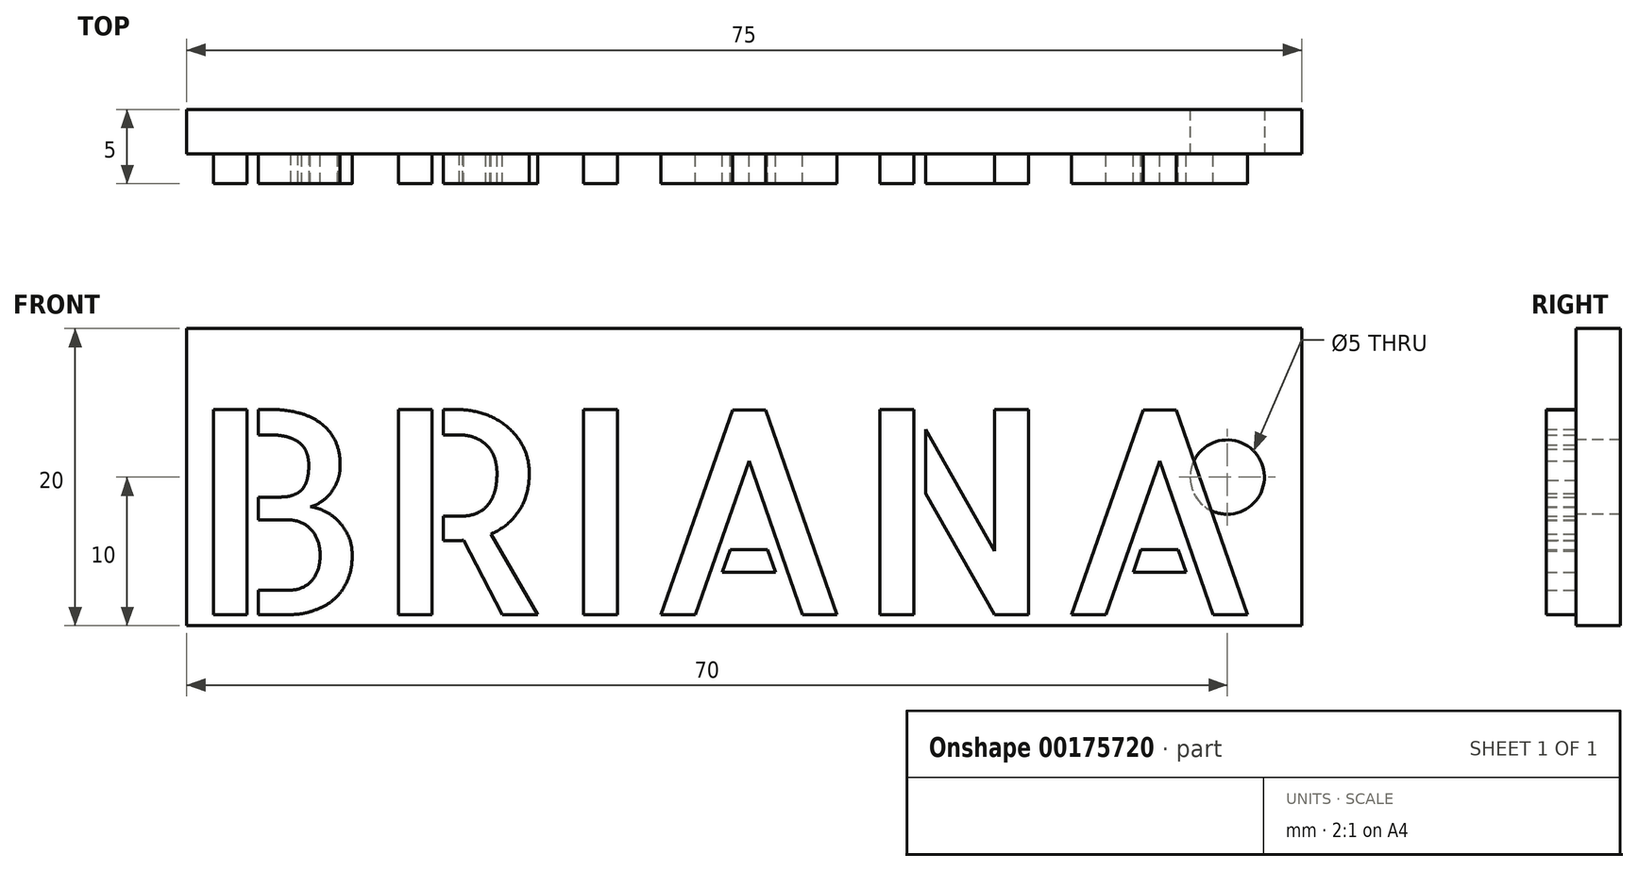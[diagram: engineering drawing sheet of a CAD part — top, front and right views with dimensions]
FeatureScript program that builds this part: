
annotation { "Feature Type Name" : "Feature", "Feature Type Description" : "" }
export const myFeature = defineFeature(function(context is Context, id is Id, definition is map)
    precondition{}
    {
        {
            var Q0;
            Q0=qCreatedBy(makeId("Front.planeOp"),FACE);
            var sketch = newSketch(context, id + "F0", { "sketchPlane" : qUnion([Q0])});
            skLineSegment(sketch, "E0.bottom", {"start": v(0, 0) * mm, "end": v(75, 0) * mm});
            skLineSegment(sketch, "E0.top", {"start": v(0, -20) * mm, "end": v(75, -20) * mm});
            skLineSegment(sketch, "E0.left", {"start": v(0, 0) * mm, "end": v(0, -20) * mm});
            skLineSegment(sketch, "E0.right", {"start": v(75, 0) * mm, "end": v(75, -20) * mm});
            skCircle(sketch, "E1", {"center": v(70, -10) * mm, "radius": 2.5 * mm});
            skSolve(sketch);
        }
        {
            var Q0;
            Q0=makeQuery(id+"F0.imprint","IMPRINT",FACE,{"disambiguationData":[TD([[makeQuery(id+"F0.imprint","IMPRINT",EDGE,{"derivedFrom":sQuery(id+"F0.wireOp",EDGE,"E0.bottom")}),-1.0]])]});
            extrude(context, id + "F1", {"entities" : qUnion([Q0]), "oppositeDirection" : true, "depth" : 3 * mm});
        }
        {
            var Q0;
            Q0=makeQuery(id+"F0.imprint","IMPRINT",FACE,{"disambiguationData":[TD([[makeQuery(id+"F0.imprint","IMPRINT",EDGE,{"derivedFrom":sQuery(id+"F0.wireOp",EDGE,"E0.bottom")}),-1.0]])]});
            var sketch = newSketch(context, id + "F2", { "sketchPlane" : qUnion([Q0])});
            skText(sketch, "E2", { "text": "BRIANA", "fontName": "AllertaStencil-Regular.ttf"});
            const initialGuessF2  = {"E2": [0, -0.01926, 1, 0, 0.01381]};
            skSetInitialGuess(sketch, initialGuessF2);
            skSolve(sketch);
        }
        {
            var Q0;
            Q0 = qSketchRegion(id + "F2", true);
            extrude(context, id + "F3", {"entities" : qUnion([Q0]), "depth" : 2 * mm});
        }
    });
